AUTODESK INVENTOR PART (.ipt)
format: ipt  version: 2017 (Build 210142000, 142)  size: 113,664 bytes
history: native  units: mm
features: other x27, extrude x2, sketch x1, projected_geometry x1
ambient origin geometry x7: Origin, YZ Plane, XZ Plane, X Axis, Y Axis, Z Axis, Center Point
bodies: Solid1 (feature_tree)
feature tree (31):
  other  "Table"
  other  "JuctionBox150x150x80mm"
  other  "JuctionBox150x150x120mm"
  other  "JuctionBox150x200x80mm"
  other  "JuctionBox150x200x120mm"
  other  "JuctionBox200x200x80mm"
  other  "JuctionBox200x200x120mm"
  other  "JuctionBox150x300x80mm"
  other  "JuctionBox150x300x120mm"
  other  "JuctionBox200x300x80mm"
  other  "JuctionBox200x300x120mm"
  other  "JuctionBox300x300x120mm"
  other  "JuctionBox150x400x120mm"
  other  "JuctionBox200x400x80mm"
  other  "JuctionBox200x400x120mm"
  other  "JuctionBox300x400x120mm"
  other  "JuctionBox400x400x120mm"
  other  "JuctionBox200x500x120mm"
  other  "JuctionBox300x500x120mm"
  other  "JuctionBox200x600x80mm"
  other  "JuctionBox200x600x120mm"
  other  "JuctionBox300x600x120mm"
  other  "JuctionBox400x600x120mm"
  other  "JuctionBox200x800x120mm"
  other  "JuctionBox400x800x120mm"
  other  "FirstSketch"
  extrude  "Extrusion1"  TaperAngle=0.0deg  [1 undecoded]
  extrude  "Extrusion3"  Depth=2.0mm
  other  "XY Ground Plane"
  sketch  "Sketch4"  dims[d3=10.0mm d6=0.0mm d9=2.0mm d10=40.0mm d11=0.0mm d25=0.0mm]
  projected_geometry  "Projected Loop1"
note: 1 required parameter value undecoded (feature->parameter linkage not recoverable at this tier; creation-order binding heuristic only, values carry confidence <= 0.55)
